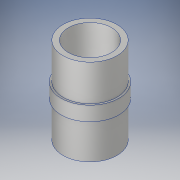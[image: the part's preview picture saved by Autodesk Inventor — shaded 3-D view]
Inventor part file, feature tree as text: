
AUTODESK INVENTOR PART (.ipt)
format: ipt  version: 2017 SP1 (Build 210196100, 196)  size: 130,560 bytes
history: native  units: in
note: dims shown in document units (in); Inventor stores cm internally (conversion verified against a paired STEP export)
features: extrude x3, sketch x3
ambient origin geometry x8: Origin, YZ Plane, XZ Plane, XY Plane, X Axis, Y Axis, Z Axis, Center Point
bodies: Solid1 (feature_tree)
feature tree (6):
  extrude  "Extrusion1"  Depth=4.0in
  extrude  "Extrusion2"  Depth=2.0in
  extrude  "Extrusion3"  Depth=5.0in TaperAngle=0.0deg
  sketch  "Sketch1"  dims[d0=8.0in d1=4.0in]
  sketch  "Sketch2"  dims[d2=2.0in d3=0.0in d4=7.5in]
  sketch  "Sketch3"  dims[d5=6.0in d6=5.0in d7=0.0in d8=6.0in d9=7.5in d10=5.0in d11=0.0in]
